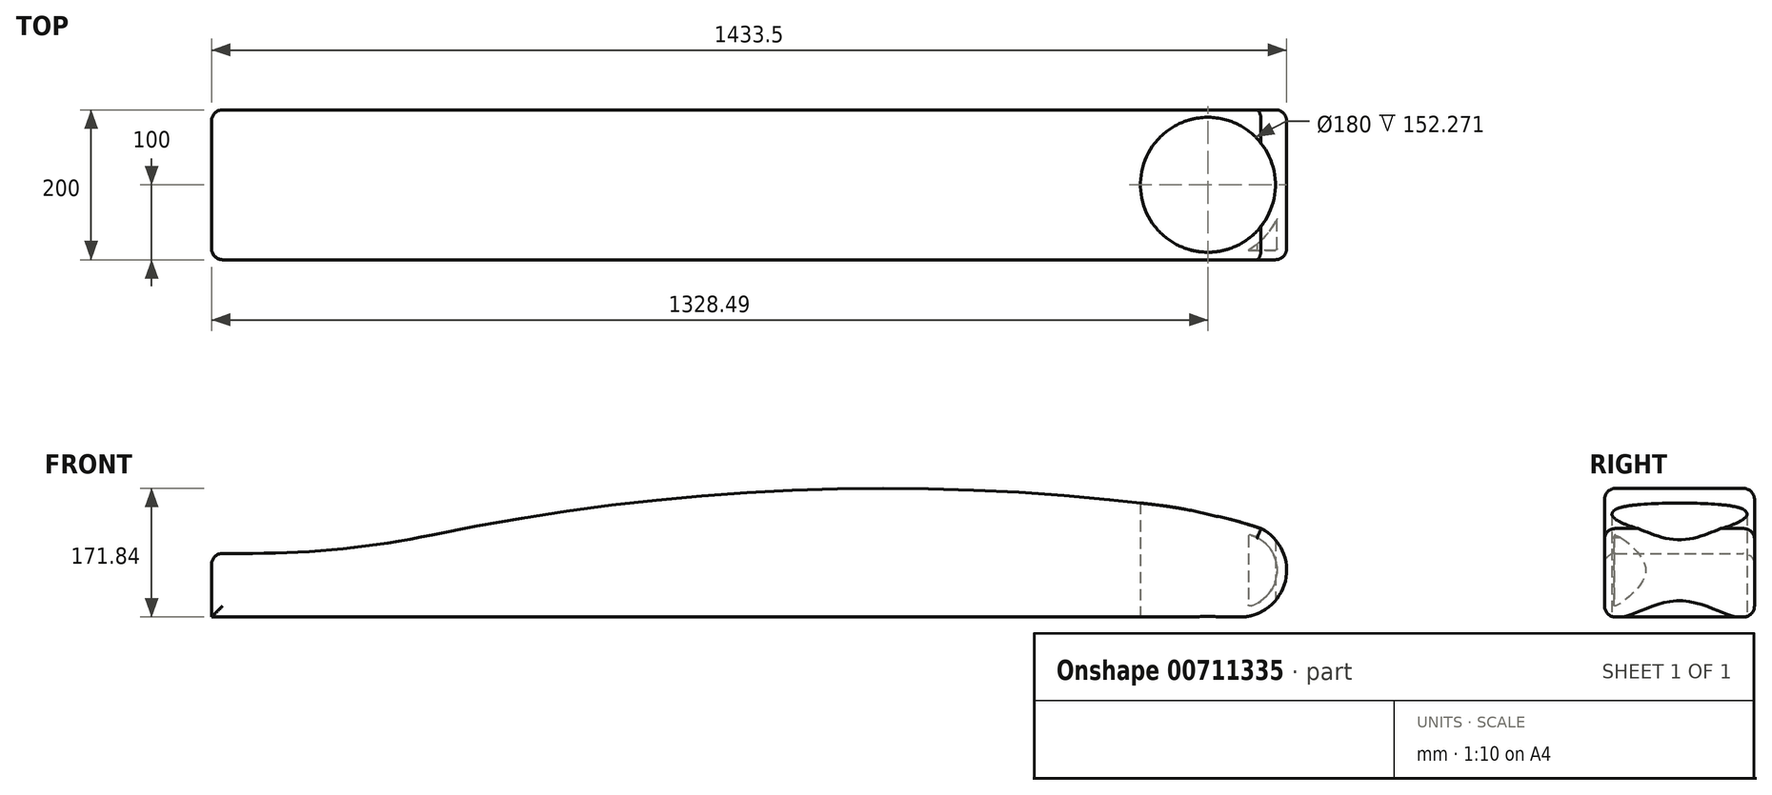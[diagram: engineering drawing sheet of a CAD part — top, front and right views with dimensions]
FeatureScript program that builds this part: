
annotation { "Feature Type Name" : "Feature", "Feature Type Description" : "" }
export const myFeature = defineFeature(function(context is Context, id is Id, definition is map)
    precondition{}
    {
        {
            var Q0;
            Q0=qCreatedBy(makeId("Front.planeOp"),FACE);
            var sketch = newSketch(context, id + "F0", { "sketchPlane" : qUnion([Q0])});
            skLineSegment(sketch, "E0", {"start": v(-1022, 0) * mm, "end": v(349, 0) * mm});
            skLineSegment(sketch, "E1", {"start": v(-1022, 0) * mm, "end": v(-1022, 85.03) * mm});
            skPoint(sketch, "E2.visualSharp", {"position": v(572.1, 0) * mm});
            skArc(sketch, "E2.filletArc", {"start": v(349, 0) * mm, "mid": v(409.77, 47.9) * mm, "end": v(377.37, 118.19) * mm});
            skLineSegment(sketch, "E3", {"start": v(-1022, 85.03) * mm, "end": v(-966.96, 85.03) * mm});
            skArc(sketch, "E4", {"start": v(-966.96, 85.03) * mm, "mid": v(-846.7, 91.2) * mm, "end": v(-727.73, 109.66) * mm});
            skArc(sketch, "E5", {"start": v(235.61, 150) * mm, "mid": v(307.3, 137.67) * mm, "end": v(377.37, 118.19) * mm});
            skArc(sketch, "E6", {"start": v(-727.73, 109.66) * mm, "mid": v(-247.7, 169.25) * mm, "end": v(235.61, 150) * mm});
            skLineSegment(sketch, "E7", {"start": v(349, 0) * mm, "end": v(349, 127) * mm});
            skLineSegment(sketch, "E8", {"start": v(377.37, 118.19) * mm, "end": v(377.37, 6.81) * mm});
            skPoint(sketch, "E9.startSnap0", {"position": v(377.37, 62.5) * mm});
            skLineSegment(sketch, "E10", {"start": v(377.37, 62.5) * mm, "end": v(411.5, 62.5) * mm});
            skSolve(sketch);
        }
        {
            var Q0;
            Q0 = qSketchRegion(id + "F0", true);
            extrude(context, id + "F1", {"entities" : qUnion([Q0]), "depth" : 200 * mm, "offsetDistance" : 25 * mm});
        }
        {
            var Q0;
            Q0=qCreatedBy(makeId("Top.planeOp"),FACE);
            var sketch = newSketch(context, id + "F2", { "sketchPlane" : qUnion([Q0])});
            skLineSegment(sketch, "E11.0", {"start": v(235.61, -200) * mm, "end": v(235.61, 0) * mm});
            skLineSegment(sketch, "E12.0", {"start": v(377.37, -200) * mm, "end": v(377.37, 0) * mm});
            skLineSegment(sketch, "E13", {"start": v(235.61, -100) * mm, "end": v(377.37, -100) * mm});
            skCircle(sketch, "E14", {"center": v(306.5, -100) * mm, "radius": 90 * mm});
            skSolve(sketch);
        }
        {
            var Q0;
            Q0 = qSketchRegion(id + "F2", true);
            extrude(context, id + "F3", {"entities" : qUnion([Q0]), "operationType" : NewBodyOperationType.REMOVE, "endBound" : BoundingType.THROUGH_ALL, "depth" : 25 * mm, "offsetDistance" : 25 * mm});
        }
        {
            var Q0;
            Q0=makeQuery(id+"F1.opExtrude","CAP_EDGE",EDGE,{"disambiguationData":[OSD([sQuery(id+"F0.wireOp",EDGE,"E6")])],"isStart":true});
            var Q1;
            Q1=makeQuery(id+"F1.opExtrude","CAP_EDGE",EDGE,{"disambiguationData":[OSD([sQuery(id+"F0.wireOp",EDGE,"E6")])],"isStart":false});
            var Q2;
            Q2=makeQuery(id+"F1.opExtrude","SWEPT_EDGE",EDGE,{"disambiguationData":[OSD([sQuery(id+"F0.wireOp",EDGE,"E1"),sQuery(id+"F0.wireOp",EDGE,"E3")])]});
            var Q3;
            Q3=makeQuery(id+"F1.opExtrude","CAP_EDGE",EDGE,{"disambiguationData":[OSD([sQuery(id+"F0.wireOp",EDGE,"E1")])],"isStart":false});
            var Q4;
            Q4=makeQuery(id+"F1.opExtrude","CAP_EDGE",EDGE,{"disambiguationData":[OSD([sQuery(id+"F0.wireOp",EDGE,"E1")])],"isStart":true});
            var Q5;
            Q5=makeQuery(id+"F1.opExtrude","CAP_EDGE",EDGE,{"disambiguationData":[OSD([sQuery(id+"F0.wireOp",EDGE,"E5")])],"isStart":true});
            var Q6;
            Q6=makeQuery(id+"F1.opExtrude","CAP_EDGE",EDGE,{"disambiguationData":[OSD([sQuery(id+"F0.wireOp",EDGE,"E5")])],"isStart":false});
            var Q7;
            Q7=makeQuery(id+"F1.opExtrude","CAP_EDGE",EDGE,{"disambiguationData":[OSD([sQuery(id+"F0.wireOp",EDGE,"E2.filletArc")])],"isStart":true});
            var Q8;
            Q8=makeQuery(id+"F1.opExtrude","CAP_EDGE",EDGE,{"disambiguationData":[OSD([sQuery(id+"F0.wireOp",EDGE,"E2.filletArc")])],"isStart":false});
            fillet(context, id + "F4", {"entities" : qUnion([Q0, Q1, Q2, Q3, Q4, Q5, Q6, Q7, Q8]), "radius" : 15 * mm, "tangentPropagation" : true, "allowEdgeOverflow" : false});
        }
        {
            var Q0;
            Q0=makeQuery(id+"F1.opExtrude","SWEPT_FACE",FACE,{"disambiguationData":[OSD([sQuery(id+"F0.wireOp",EDGE,"E6")])]});
            var Q1;
            Q1=makeQuery(id+"F1.opExtrude","SWEPT_BODY",BODY,{"disambiguationData":[OSD([sQuery(id+"F0.wireOp",EDGE,"E0"),sQuery(id+"F0.wireOp",EDGE,"E1"),sQuery(id+"F0.wireOp",EDGE,"E2.filletArc"),sQuery(id+"F0.wireOp",EDGE,"E3"),sQuery(id+"F0.wireOp",EDGE,"E4"),sQuery(id+"F0.wireOp",EDGE,"E5"),sQuery(id+"F0.wireOp",EDGE,"E6")])]});
            shell(context, id + "F5", {"isHollow" : true, "entities" : qUnion([Q0]), "parts" : qUnion([Q1]), "thickness" : 12.7 * mm});
        }
    });
